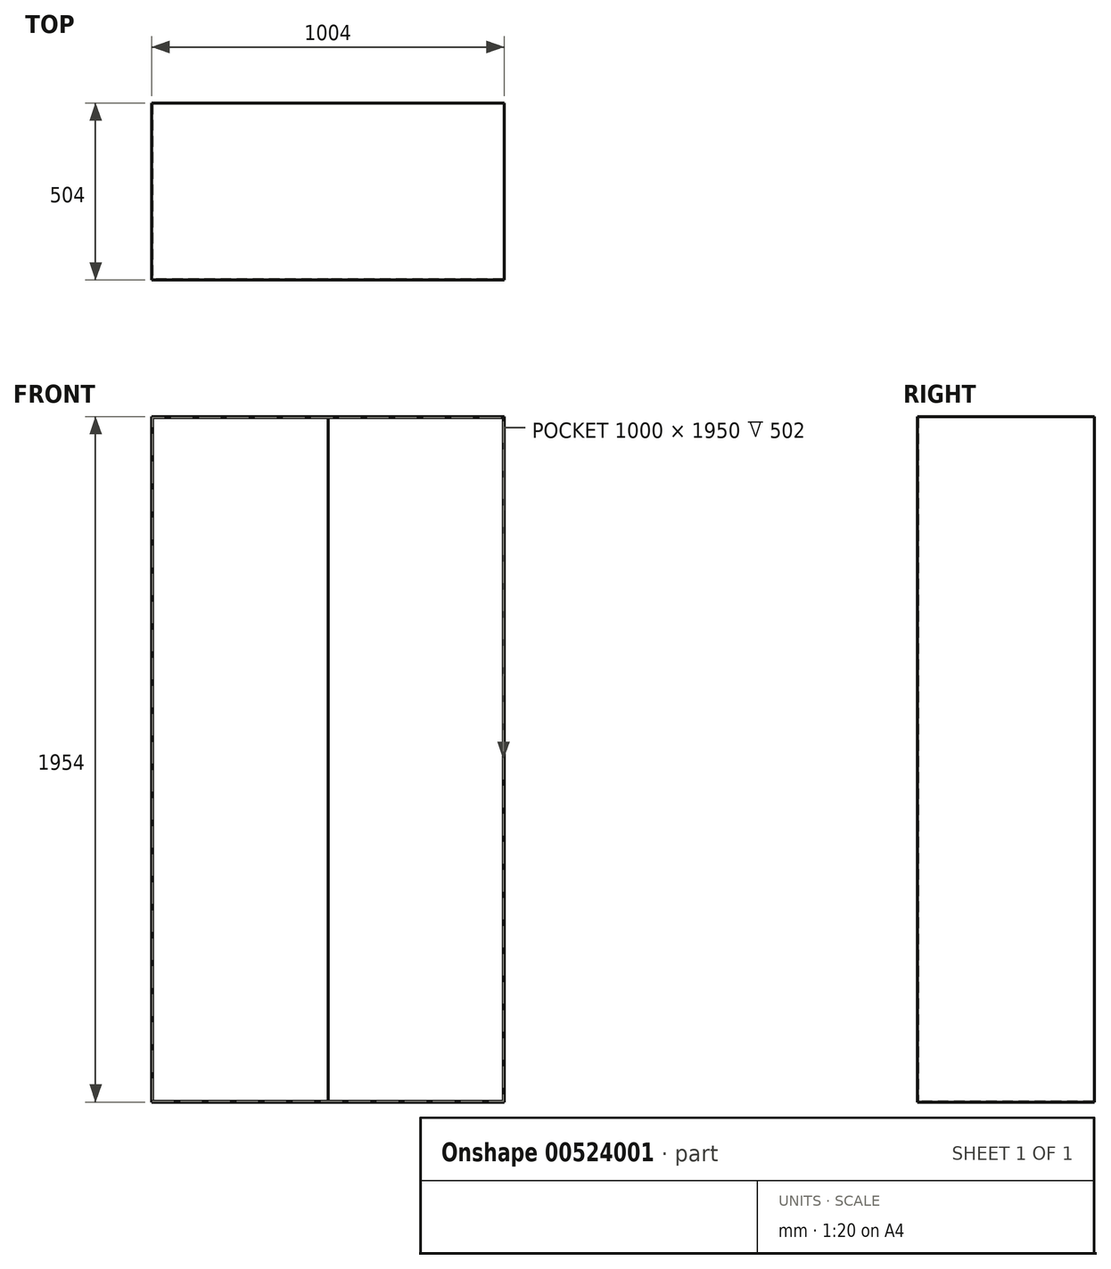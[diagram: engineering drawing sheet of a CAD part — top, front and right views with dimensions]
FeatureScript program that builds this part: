
annotation { "Feature Type Name" : "Feature", "Feature Type Description" : "" }
export const myFeature = defineFeature(function(context is Context, id is Id, definition is map)
    precondition{}
    {
        {
            var Q0;
            Q0=qCreatedBy(makeId("Top.planeOp"),FACE);
            var sketch = newSketch(context, id + "F0", { "sketchPlane" : qUnion([Q0])});
            skLineSegment(sketch, "E0.bottom", {"start": v(500, 250) * mm, "end": v(-500, 250) * mm});
            skLineSegment(sketch, "E0.top", {"start": v(500, -250) * mm, "end": v(-500, -250) * mm});
            skLineSegment(sketch, "E0.left", {"start": v(500, 250) * mm, "end": v(500, -250) * mm});
            skLineSegment(sketch, "E0.right", {"start": v(-500, 250) * mm, "end": v(-500, -250) * mm});
            skPoint(sketch, "E0.middle", {"position": v(0, 0) * mm});
            skLineSegment(sketch, "E1.0", {"start": v(502, 252) * mm, "end": v(-502, 252) * mm});
            skLineSegment(sketch, "E1.1", {"start": v(502, 252) * mm, "end": v(502, -252) * mm});
            skLineSegment(sketch, "E1.2", {"start": v(502, -252) * mm, "end": v(-502, -252) * mm});
            skLineSegment(sketch, "E1.3", {"start": v(-502, 252) * mm, "end": v(-502, -252) * mm});
            skLineSegment(sketch, "E2", {"start": v(-500, -250) * mm, "end": v(-500, -252) * mm});
            skLineSegment(sketch, "E3", {"start": v(500, -250) * mm, "end": v(500, -252) * mm});
            skLineSegment(sketch, "E4", {"start": v(0, -250) * mm, "end": v(0, -252) * mm});
            skSolve(sketch);
        }
        {
            var Q0;
            Q0=makeQuery(id+"F0.imprint","IMPRINT",FACE,{"disambiguationData":[TD([[makeQuery(id+"F0.imprint","IMPRINT",EDGE,{"derivedFrom":sQuery(id+"F0.wireOp",EDGE,"E0.bottom")}),1.0]])]});
            var Q1;
            Q1=makeQuery(id+"F0.imprint","IMPRINT",FACE,{"disambiguationData":[TD([[makeQuery(id+"F0.imprint","IMPRINT",EDGE,{"derivedFrom":sQuery(id+"F0.wireOp",EDGE,"E0.bottom")}),-1.0]])]});
            var Q2;
            {var subQ0=sQuery(id+"F0.wireOp",EDGE,"E3");Q2=makeQuery(id+"F0.imprint","IMPRINT",FACE,{"disambiguationData":[TD([[makeQuery(id+"F0.imprint","IMPRINT",EDGE,{"derivedFrom":subQ0}),-1.0]])]});}
            var Q3;
            {var subQ0=sQuery(id+"F0.wireOp",EDGE,"E2");Q3=makeQuery(id+"F0.imprint","IMPRINT",FACE,{"disambiguationData":[TD([[makeQuery(id+"F0.imprint","IMPRINT",EDGE,{"derivedFrom":subQ0}),1.0]])]});}
            extrude(context, id + "F1", {"entities" : qUnion([Q0, Q1, Q2, Q3]), "oppositeDirection" : true, "depth" : 2 * mm, "offsetDistance" : 25 * mm});
        }
        {
            var Q0;
            Q0=makeQuery(id+"F0.imprint","IMPRINT",FACE,{"disambiguationData":[TD([[makeQuery(id+"F0.imprint","IMPRINT",EDGE,{"derivedFrom":sQuery(id+"F0.wireOp",EDGE,"E0.bottom")}),-1.0]])]});
            extrude(context, id + "F2", {"entities" : qUnion([Q0]), "operationType" : NewBodyOperationType.ADD, "depth" : 1950 * mm, "offsetDistance" : 25 * mm});
        }
        {
            var Q0;
            Q0=makeQuery(id+"F2.opExtrude","CAP_FACE",FACE,{"disambiguationData":[OSD([sQuery(id+"F0.wireOp",EDGE,"E0.bottom"),sQuery(id+"F0.wireOp",EDGE,"E0.left"),sQuery(id+"F0.wireOp",EDGE,"E0.right"),sQuery(id+"F0.wireOp",EDGE,"E1.0"),sQuery(id+"F0.wireOp",EDGE,"E1.1"),sQuery(id+"F0.wireOp",EDGE,"E1.2"),sQuery(id+"F0.wireOp",EDGE,"E1.3"),sQuery(id+"F0.wireOp",EDGE,"E2"),sQuery(id+"F0.wireOp",EDGE,"E3")])],"isStart":false});
            var sketch = newSketch(context, id + "F3", { "sketchPlane" : qUnion([Q0])});
            skLineSegment(sketch, "E5", {"start": v(-502, -252) * mm, "end": v(502, -252) * mm});
            skSolve(sketch);
        }
        {
            var Q0;
            Q0=makeQuery(id+"F3.imprint","IMPRINT",FACE,{"disambiguationData":[TD([[makeQuery(id+"F3.imprint","IMPRINT",EDGE,{"derivedFrom":makeQuery(id+"F2.opExtrude","CAP_EDGE",EDGE,{"disambiguationData":[OSD([sQuery(id+"F0.wireOp",EDGE,"E0.bottom")])],"isStart":false})}),1.0]])]});
            var Q1;
            Q1=makeQuery(id+"F3.imprint","IMPRINT",FACE,{"disambiguationData":[TD([[makeQuery(id+"F3.imprint","IMPRINT",EDGE,{"derivedFrom":makeQuery(id+"F2.opExtrude","CAP_EDGE",EDGE,{"disambiguationData":[OSD([sQuery(id+"F0.wireOp",EDGE,"E0.bottom")])],"isStart":false})}),-1.0]])]});
            extrude(context, id + "F4", {"entities" : qUnion([Q0, Q1]), "operationType" : NewBodyOperationType.ADD, "depth" : 2 * mm, "offsetDistance" : 25 * mm});
        }
        {
            var Q0;
            {var subQ0=sQuery(id+"F0.wireOp",EDGE,"E2");Q0=makeQuery(id+"F0.imprint","IMPRINT",FACE,{"disambiguationData":[TD([[makeQuery(id+"F0.imprint","IMPRINT",EDGE,{"derivedFrom":subQ0}),1.0]])]});}
            extrude(context, id + "F5", {"entities" : qUnion([Q0]), "endBound" : BoundingType.UP_TO_NEXT, "depth" : 25 * mm, "offsetDistance" : 25 * mm});
        }
        {
            var Q0;
            {var subQ0=sQuery(id+"F0.wireOp",EDGE,"E3");Q0=makeQuery(id+"F0.imprint","IMPRINT",FACE,{"disambiguationData":[TD([[makeQuery(id+"F0.imprint","IMPRINT",EDGE,{"derivedFrom":subQ0}),-1.0]])]});}
            extrude(context, id + "F6", {"entities" : qUnion([Q0]), "endBound" : BoundingType.UP_TO_NEXT, "depth" : 25 * mm, "offsetDistance" : 25 * mm});
        }
    });
